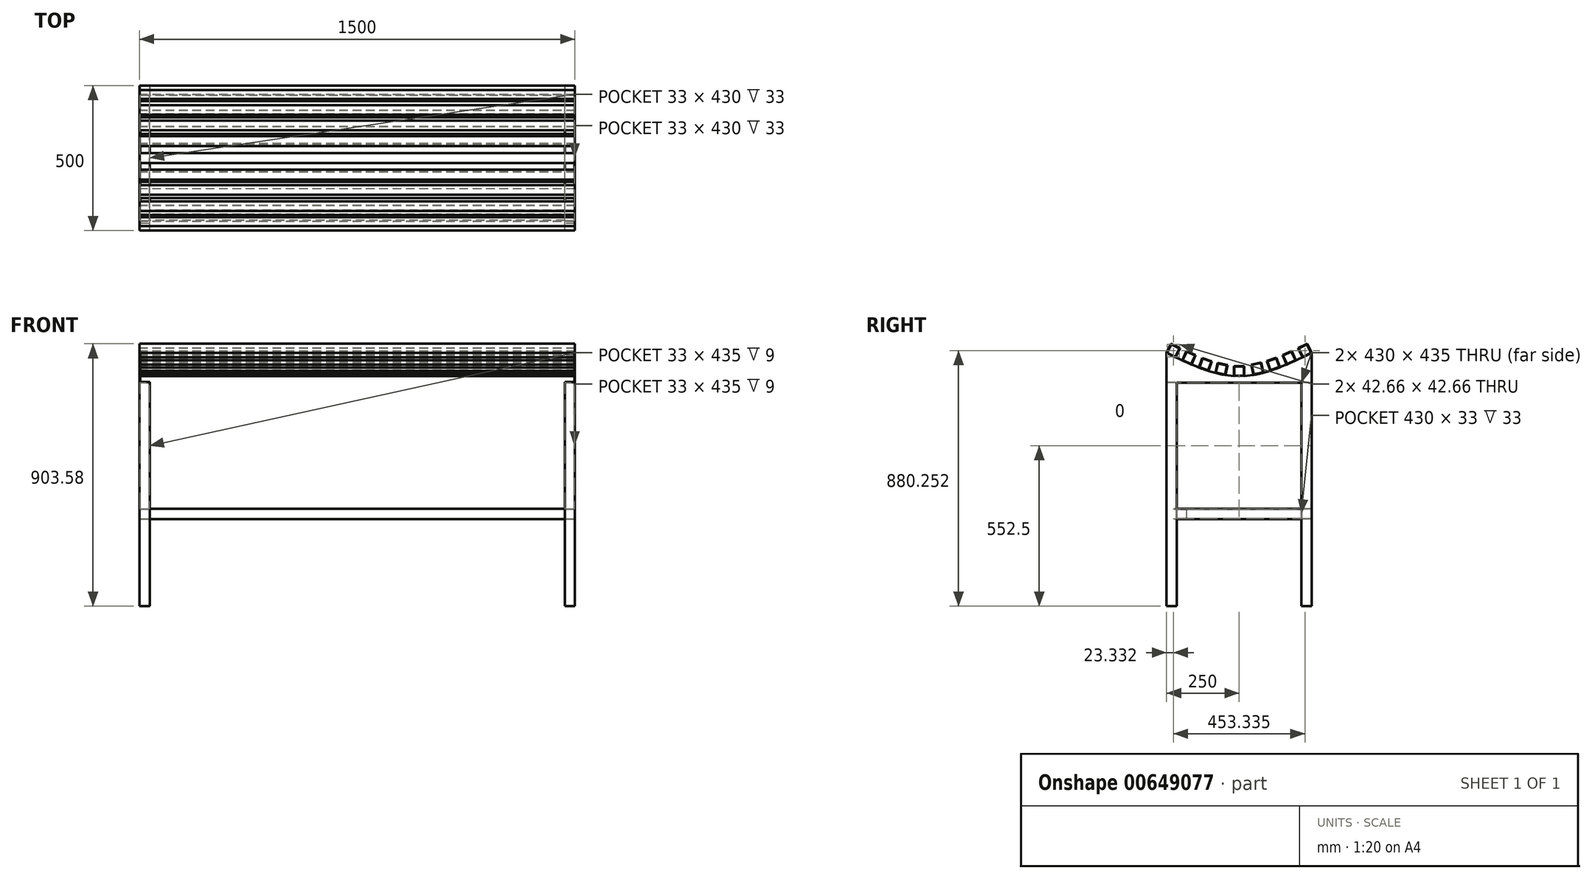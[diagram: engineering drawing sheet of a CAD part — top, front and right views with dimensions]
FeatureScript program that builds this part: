
annotation { "Feature Type Name" : "Feature", "Feature Type Description" : "" }
export const myFeature = defineFeature(function(context is Context, id is Id, definition is map)
    precondition{}
    {
        {
            var Q0;
            Q0=qCreatedBy(makeId("Right.planeOp"),FACE);
            var sketch = newSketch(context, id + "F0", { "sketchPlane" : qUnion([Q0])});
            skLineSegment(sketch, "E0.bottom", {"start": v(-250, -50) * mm, "end": v(250, -50) * mm});
            skLineSegment(sketch, "E0.top", {"start": v(-250, 50) * mm, "end": v(250, 50) * mm});
            skLineSegment(sketch, "E0.left", {"start": v(-250, -50) * mm, "end": v(-250, 50) * mm});
            skLineSegment(sketch, "E0.right", {"start": v(250, -50) * mm, "end": v(250, 50) * mm});
            skPoint(sketch, "E0.middle", {"position": v(0, 0) * mm});
            skLineSegment(sketch, "E1", {"start": v(0, 50) * mm, "end": v(0, -30) * mm, "construction": true});
            skFitSpline(sketch, "E2", {"points": [v(250, 50) * mm, v(0, -30) * mm, v(-250, 50) * mm], "startDerivative": vector(-500, -240) * mm, "endDerivative": vector(-500, 240) * mm});
            skSolve(sketch);
        }
        {
            var Q0;
            Q0=makeQuery(id+"F0.imprint","IMPRINT",FACE,{"disambiguationData":[TD([[makeQuery(id+"F0.imprint","IMPRINT",EDGE,{"derivedFrom":sQuery(id+"F0.wireOp",EDGE,"E0.bottom")}),1.0]])]});
            extrude(context, id + "F1", {"entities" : qUnion([Q0]), "depth" : 2 * mm, "offsetDistance" : 25 * mm});
        }
        {
            var Q0;
            Q0=makeQuery(id+"F1.opExtrude","SWEPT_FACE",FACE,{"disambiguationData":[OSD([sQuery(id+"F0.wireOp",EDGE,"E0.bottom")])]});
            var sketch = newSketch(context, id + "F2", { "sketchPlane" : qUnion([Q0])});
            skLineSegment(sketch, "E3.bottom", {"start": v(0, 250) * mm, "end": v(35, 250) * mm});
            skLineSegment(sketch, "E3.top", {"start": v(0, -250) * mm, "end": v(35, -250) * mm});
            skLineSegment(sketch, "E3.left", {"start": v(0, 250) * mm, "end": v(0, -250) * mm});
            skLineSegment(sketch, "E3.right", {"start": v(35, 250) * mm, "end": v(35, -250) * mm});
            skSolve(sketch);
        }
        {
            var Q0;
            Q0 = qSketchRegion(id + "F2", true);
            extrude(context, id + "F3", {"entities" : qUnion([Q0]), "operationType" : NewBodyOperationType.ADD, "depth" : 2 * mm, "offsetDistance" : 25 * mm});
        }
        {
            var Q0;
            Q0=makeQuery(id+"F1.opExtrude","SWEPT_BODY",BODY,{"disambiguationData":[OSD([sQuery(id+"F0.wireOp",EDGE,"E0.bottom"),sQuery(id+"F0.wireOp",EDGE,"E0.left"),sQuery(id+"F0.wireOp",EDGE,"E0.right"),sQuery(id+"F0.wireOp",EDGE,"E2")])]});
            var Q1;
            Q1=makeQuery(id+"F3.opExtrude","SWEPT_FACE",FACE,{"disambiguationData":[OSD([sQuery(id+"F2.wireOp",EDGE,"E3.right")])]});
            mirror(context, id + "F4", {"entities" : qUnion([Q0]), "mirrorPlane" : qUnion([Q1])});
        }
        {
            var Q0;
            Q0=makeQuery(id+"F4.opPattern","COPY",BODY,{"derivedFrom":makeQuery(id+"F1.opExtrude","SWEPT_BODY",BODY,{"disambiguationData":[OSD([sQuery(id+"F0.wireOp",EDGE,"E0.bottom"),sQuery(id+"F0.wireOp",EDGE,"E0.left"),sQuery(id+"F0.wireOp",EDGE,"E0.right"),sQuery(id+"F0.wireOp",EDGE,"E2")])]}),"instanceName":"1"});
            transform(context, id + "F5", {"entities" : qUnion([Q0]), "transformType" : TransformType.TRANSLATION_3D, "dx" : 1430 * mm, "dy" : 0 * mm, "dz" : 0 * mm, "makeCopy" : false});
        }
        {
            var Q0;
            Q0=makeQuery(id+"F3.boolean.opBoolean","MERGE",FACE,{"derivedFrom":[makeQuery(id+"F1.opExtrude","CAP_FACE",FACE,{"disambiguationData":[OSD([sQuery(id+"F0.wireOp",EDGE,"E0.bottom"),sQuery(id+"F0.wireOp",EDGE,"E0.left"),sQuery(id+"F0.wireOp",EDGE,"E0.right"),sQuery(id+"F0.wireOp",EDGE,"E2")])],"isStart":true}),makeQuery(id+"F3.opExtrude","SWEPT_FACE",FACE,{"disambiguationData":[OSD([sQuery(id+"F2.wireOp",EDGE,"E3.left")])]})]});
            var sketch = newSketch(context, id + "F6", { "sketchPlane" : qUnion([Q0])});
            skLineSegment(sketch, "E4", {"start": v(0, -52) * mm, "end": v(0, -30) * mm, "construction": true});
            skLineSegment(sketch, "E5", {"start": v(0, -30) * mm, "end": v(0, -12.5) * mm, "construction": true});
            skLineSegment(sketch, "E6.bottom", {"start": v(17.5, -30) * mm, "end": v(-17.5, -30) * mm});
            skLineSegment(sketch, "E6.top", {"start": v(17.5, 5) * mm, "end": v(-17.5, 5) * mm});
            skLineSegment(sketch, "E6.left", {"start": v(17.5, -30) * mm, "end": v(17.5, 5) * mm});
            skLineSegment(sketch, "E6.right", {"start": v(-17.5, -30) * mm, "end": v(-17.5, 5) * mm});
            skPoint(sketch, "E6.middle", {"position": v(0, -12.5) * mm});
            skLineSegment(sketch, "E7.bottom", {"start": v(16, -28.5) * mm, "end": v(-16, -28.5) * mm});
            skLineSegment(sketch, "E7.top", {"start": v(16, 3.5) * mm, "end": v(-16, 3.5) * mm});
            skLineSegment(sketch, "E7.left", {"start": v(16, -28.5) * mm, "end": v(16, 3.5) * mm});
            skLineSegment(sketch, "E7.right", {"start": v(-16, -28.5) * mm, "end": v(-16, 3.5) * mm});
            skSolve(sketch);
        }
        {
            var Q0;
            Q0 = qSketchRegion(id + "F6", true);
            extrude(context, id + "F7", {"entities" : qUnion([Q0]), "operationType" : NewBodyOperationType.ADD, "oppositeDirection" : true, "depth" : 1500 * mm, "offsetDistance" : 25 * mm});
        }
        {
            var Q0;
            Q0=makeQuery(id+"F7.boolean.opBoolean","MERGE",FACE,{"derivedFrom":[makeQuery(id+"F3.boolean.opBoolean","MERGE",FACE,{"derivedFrom":[makeQuery(id+"F1.opExtrude","CAP_FACE",FACE,{"disambiguationData":[OSD([sQuery(id+"F0.wireOp",EDGE,"E0.bottom"),sQuery(id+"F0.wireOp",EDGE,"E0.left"),sQuery(id+"F0.wireOp",EDGE,"E0.right"),sQuery(id+"F0.wireOp",EDGE,"E2")])],"isStart":true}),makeQuery(id+"F3.opExtrude","SWEPT_FACE",FACE,{"disambiguationData":[OSD([sQuery(id+"F2.wireOp",EDGE,"E3.left")])]})]}),makeQuery(id+"F7.opExtrude","CAP_FACE",FACE,{"disambiguationData":[OSD([sQuery(id+"F6.wireOp",EDGE,"E6.bottom"),sQuery(id+"F6.wireOp",EDGE,"E6.top"),sQuery(id+"F6.wireOp",EDGE,"E6.left"),sQuery(id+"F6.wireOp",EDGE,"E6.right"),sQuery(id+"F6.wireOp",EDGE,"E7.bottom"),sQuery(id+"F6.wireOp",EDGE,"E7.top"),sQuery(id+"F6.wireOp",EDGE,"E7.left"),sQuery(id+"F6.wireOp",EDGE,"E7.right")])],"isStart":true})]});
            var sketch = newSketch(context, id + "F8", { "sketchPlane" : qUnion([Q0])});
            skLineSegment(sketch, "E8", {"start": v(-250, 50) * mm, "end": v(-218.42, 34.92) * mm});
            skLineSegment(sketch, "E9", {"start": v(-218.42, 34.92) * mm, "end": v(-203.34, 66.5) * mm});
            skLineSegment(sketch, "E10", {"start": v(-203.34, 66.5) * mm, "end": v(-234.92, 81.58) * mm});
            skLineSegment(sketch, "E11", {"start": v(-250, 50) * mm, "end": v(-234.92, 81.58) * mm});
            skLineSegment(sketch, "E12", {"start": v(-250, 50) * mm, "end": v(-203.34, 66.5) * mm, "construction": true});
            skLineSegment(sketch, "E13", {"start": v(-234.92, 81.58) * mm, "end": v(-218.42, 34.92) * mm, "construction": true});
            skLineSegment(sketch, "E14", {"start": v(-219.13, 74.04) * mm, "end": v(-219.77, 72.7) * mm, "construction": true});
            skLineSegment(sketch, "E15", {"start": v(-219.77, 72.7) * mm, "end": v(-234.21, 79.58) * mm});
            skLineSegment(sketch, "E16", {"start": v(-234.21, 79.58) * mm, "end": v(-248, 50.7) * mm});
            skLineSegment(sketch, "E17", {"start": v(-248, 50.7) * mm, "end": v(-219.12, 36.92) * mm});
            skLineSegment(sketch, "E18", {"start": v(-219.12, 36.92) * mm, "end": v(-205.34, 65.8) * mm});
            skLineSegment(sketch, "E19", {"start": v(-205.34, 65.8) * mm, "end": v(-219.77, 72.7) * mm});
            skSolve(sketch);
        }
        {
            var Q0;
            Q0 = qSketchRegion(id + "F8", true);
            extrude(context, id + "F9", {"entities" : qUnion([Q0]), "oppositeDirection" : true, "depth" : 1500 * mm, "offsetDistance" : 25 * mm});
        }
        {
            var Q0;
            Q0=makeQuery(id+"F7.boolean.opBoolean","MERGE",FACE,{"derivedFrom":[makeQuery(id+"F3.boolean.opBoolean","MERGE",FACE,{"derivedFrom":[makeQuery(id+"F1.opExtrude","CAP_FACE",FACE,{"disambiguationData":[OSD([sQuery(id+"F0.wireOp",EDGE,"E0.bottom"),sQuery(id+"F0.wireOp",EDGE,"E0.left"),sQuery(id+"F0.wireOp",EDGE,"E0.right"),sQuery(id+"F0.wireOp",EDGE,"E2")])],"isStart":true}),makeQuery(id+"F3.opExtrude","SWEPT_FACE",FACE,{"disambiguationData":[OSD([sQuery(id+"F2.wireOp",EDGE,"E3.left")])]})]}),makeQuery(id+"F7.opExtrude","CAP_FACE",FACE,{"disambiguationData":[OSD([sQuery(id+"F6.wireOp",EDGE,"E6.bottom"),sQuery(id+"F6.wireOp",EDGE,"E6.top"),sQuery(id+"F6.wireOp",EDGE,"E6.left"),sQuery(id+"F6.wireOp",EDGE,"E6.right"),sQuery(id+"F6.wireOp",EDGE,"E7.bottom"),sQuery(id+"F6.wireOp",EDGE,"E7.top"),sQuery(id+"F6.wireOp",EDGE,"E7.left"),sQuery(id+"F6.wireOp",EDGE,"E7.right")])],"isStart":true})]});
            var sketch = newSketch(context, id + "F10", { "sketchPlane" : qUnion([Q0])});
            skLineSegment(sketch, "E20", {"start": v(-250, 50) * mm, "end": v(-218.42, 34.92) * mm, "construction": true});
            skLineSegment(sketch, "E21", {"start": v(-218.42, 34.92) * mm, "end": v(-195.75, 24.37) * mm, "construction": true});
            skLineSegment(sketch, "E22", {"start": v(-195.75, 24.37) * mm, "end": v(-163.73, 10.23) * mm, "construction": true});
            skLineSegment(sketch, "E23", {"start": v(-163.73, 10.23) * mm, "end": v(-140.57, 0.83) * mm, "construction": true});
            skLineSegment(sketch, "E24", {"start": v(-140.57, 0.83) * mm, "end": v(-107.61, -10.96) * mm, "construction": true});
            skLineSegment(sketch, "E25", {"start": v(-107.61, -10.96) * mm, "end": v(-83.64, -18.07) * mm, "construction": true});
            skLineSegment(sketch, "E26", {"start": v(-83.64, -18.07) * mm, "end": v(-49.47, -25.61) * mm, "construction": true});
            skLineSegment(sketch, "E27", {"start": v(-49.47, -25.61) * mm, "end": v(-41.55, 10.23) * mm});
            skLineSegment(sketch, "E28", {"start": v(-41.55, 10.23) * mm, "end": v(-75.73, 17.78) * mm});
            skLineSegment(sketch, "E29", {"start": v(-75.73, 17.78) * mm, "end": v(-83.64, -18.07) * mm});
            skLineSegment(sketch, "E30", {"start": v(-107.61, -10.96) * mm, "end": v(-95.83, 22) * mm});
            skLineSegment(sketch, "E31", {"start": v(-95.83, 22) * mm, "end": v(-128.79, 33.78) * mm});
            skLineSegment(sketch, "E32", {"start": v(-128.79, 33.78) * mm, "end": v(-140.57, 0.83) * mm});
            skLineSegment(sketch, "E33", {"start": v(-140.57, 0.83) * mm, "end": v(-107.61, -10.96) * mm});
            skLineSegment(sketch, "E34", {"start": v(-195.75, 24.37) * mm, "end": v(-163.73, 10.23) * mm});
            skLineSegment(sketch, "E35", {"start": v(-163.73, 10.23) * mm, "end": v(-149.6, 42.25) * mm});
            skLineSegment(sketch, "E36", {"start": v(-149.6, 42.25) * mm, "end": v(-181.62, 56.39) * mm});
            skLineSegment(sketch, "E37", {"start": v(-181.62, 56.39) * mm, "end": v(-195.75, 24.37) * mm});
            skLineSegment(sketch, "E38", {"start": v(-181.62, 56.39) * mm, "end": v(-163.73, 10.23) * mm, "construction": true});
            skLineSegment(sketch, "E39", {"start": v(-195.75, 24.37) * mm, "end": v(-149.6, 42.25) * mm, "construction": true});
            skLineSegment(sketch, "E40", {"start": v(-128.79, 33.78) * mm, "end": v(-107.61, -10.96) * mm, "construction": true});
            skLineSegment(sketch, "E41", {"start": v(-95.83, 22) * mm, "end": v(-140.57, 0.83) * mm, "construction": true});
            skLineSegment(sketch, "E42", {"start": v(-75.73, 17.78) * mm, "end": v(-49.47, -25.61) * mm, "construction": true});
            skLineSegment(sketch, "E43", {"start": v(-41.55, 10.23) * mm, "end": v(-83.64, -18.07) * mm, "construction": true});
            skLineSegment(sketch, "E44", {"start": v(-165.6, 49.32) * mm, "end": v(-166.17, 47.93) * mm, "construction": true});
            skLineSegment(sketch, "E45", {"start": v(-166.17, 47.93) * mm, "end": v(-151.57, 41.49) * mm});
            skLineSegment(sketch, "E46", {"start": v(-151.57, 41.49) * mm, "end": v(-164.5, 12.21) * mm});
            skLineSegment(sketch, "E47", {"start": v(-164.5, 12.21) * mm, "end": v(-193.77, 25.14) * mm});
            skLineSegment(sketch, "E48", {"start": v(-193.77, 25.14) * mm, "end": v(-180.85, 54.41) * mm});
            skLineSegment(sketch, "E49", {"start": v(-180.85, 54.41) * mm, "end": v(-166.17, 47.93) * mm});
            skLineSegment(sketch, "E50", {"start": v(-112.3, 27.9) * mm, "end": v(-112.81, 26.48) * mm, "construction": true});
            skLineSegment(sketch, "E51", {"start": v(-112.81, 26.48) * mm, "end": v(-97.75, 21.1) * mm});
            skLineSegment(sketch, "E52", {"start": v(-97.75, 21.1) * mm, "end": v(-108.52, -9.04) * mm});
            skLineSegment(sketch, "E53", {"start": v(-108.52, -9.04) * mm, "end": v(-138.65, 1.74) * mm});
            skLineSegment(sketch, "E54", {"start": v(-138.65, 1.74) * mm, "end": v(-127.88, 31.87) * mm});
            skLineSegment(sketch, "E55", {"start": v(-127.88, 31.87) * mm, "end": v(-112.81, 26.48) * mm});
            skLineSegment(sketch, "E56", {"start": v(-58.64, 14) * mm, "end": v(-58.96, 12.54) * mm, "construction": true});
            skLineSegment(sketch, "E57", {"start": v(-58.96, 12.54) * mm, "end": v(-43.27, 9.08) * mm});
            skLineSegment(sketch, "E58", {"start": v(-43.27, 9.08) * mm, "end": v(-50.54, -23.84) * mm});
            skLineSegment(sketch, "E59", {"start": v(-50.54, -23.84) * mm, "end": v(-81.92, -16.9) * mm});
            skLineSegment(sketch, "E60", {"start": v(-81.92, -16.9) * mm, "end": v(-74.66, 16) * mm});
            skLineSegment(sketch, "E61", {"start": v(-74.66, 16) * mm, "end": v(-58.96, 12.54) * mm});
            skSolve(sketch);
        }
        {
            var Q0;
            Q0=makeQuery(id+"F10.imprint","IMPRINT",FACE,{"disambiguationData":[TD([[makeQuery(id+"F10.imprint","IMPRINT",EDGE,{"derivedFrom":sQuery(id+"F10.wireOp",EDGE,"E28")}),1.0]])]});
            var Q1;
            Q1=makeQuery(id+"F10.imprint","IMPRINT",FACE,{"disambiguationData":[TD([[makeQuery(id+"F10.imprint","IMPRINT",EDGE,{"derivedFrom":sQuery(id+"F10.wireOp",EDGE,"E30")}),1.0]])]});
            var Q2;
            Q2=makeQuery(id+"F10.imprint","IMPRINT",FACE,{"disambiguationData":[TD([[makeQuery(id+"F10.imprint","IMPRINT",EDGE,{"derivedFrom":sQuery(id+"F10.wireOp",EDGE,"E34")}),1.0]])]});
            extrude(context, id + "F11", {"entities" : qUnion([Q0, Q1, Q2]), "oppositeDirection" : true, "depth" : 1500 * mm, "offsetDistance" : 25 * mm});
        }
        {
            var Q0;
            Q0=makeQuery(id+"F7.boolean.opBoolean","MERGE",FACE,{"derivedFrom":[makeQuery(id+"F3.boolean.opBoolean","MERGE",FACE,{"derivedFrom":[makeQuery(id+"F1.opExtrude","CAP_FACE",FACE,{"disambiguationData":[OSD([sQuery(id+"F0.wireOp",EDGE,"E0.bottom"),sQuery(id+"F0.wireOp",EDGE,"E0.left"),sQuery(id+"F0.wireOp",EDGE,"E0.right"),sQuery(id+"F0.wireOp",EDGE,"E2")])],"isStart":true}),makeQuery(id+"F3.opExtrude","SWEPT_FACE",FACE,{"disambiguationData":[OSD([sQuery(id+"F2.wireOp",EDGE,"E3.left")])]})]}),makeQuery(id+"F7.opExtrude","CAP_FACE",FACE,{"disambiguationData":[OSD([sQuery(id+"F6.wireOp",EDGE,"E6.bottom"),sQuery(id+"F6.wireOp",EDGE,"E6.top"),sQuery(id+"F6.wireOp",EDGE,"E6.left"),sQuery(id+"F6.wireOp",EDGE,"E6.right"),sQuery(id+"F6.wireOp",EDGE,"E7.bottom"),sQuery(id+"F6.wireOp",EDGE,"E7.top"),sQuery(id+"F6.wireOp",EDGE,"E7.left"),sQuery(id+"F6.wireOp",EDGE,"E7.right")])],"isStart":true})]});
            var sketch = newSketch(context, id + "F12", { "sketchPlane" : qUnion([Q0])});
            skLineSegment(sketch, "E62", {"start": v(250, 50) * mm, "end": v(218.42, 34.92) * mm});
            skLineSegment(sketch, "E63", {"start": v(218.42, 34.92) * mm, "end": v(195.75, 24.37) * mm, "construction": true});
            skLineSegment(sketch, "E64", {"start": v(195.75, 24.37) * mm, "end": v(163.73, 10.23) * mm});
            skLineSegment(sketch, "E65", {"start": v(163.73, 10.23) * mm, "end": v(138.43, 0) * mm, "construction": true});
            skLineSegment(sketch, "E66", {"start": v(138.43, 0) * mm, "end": v(105.42, -11.66) * mm});
            skLineSegment(sketch, "E67", {"start": v(105.42, -11.66) * mm, "end": v(81.42, -18.65) * mm, "construction": true});
            skLineSegment(sketch, "E68", {"start": v(81.42, -18.65) * mm, "end": v(47.2, -26) * mm});
            skLineSegment(sketch, "E69", {"start": v(47.2, -26) * mm, "end": v(39.86, 8.23) * mm});
            skLineSegment(sketch, "E70", {"start": v(39.86, 8.23) * mm, "end": v(74.08, 15.57) * mm});
            skLineSegment(sketch, "E71", {"start": v(74.08, 15.57) * mm, "end": v(81.42, -18.65) * mm});
            skLineSegment(sketch, "E72", {"start": v(105.42, -11.66) * mm, "end": v(93.76, 21.34) * mm});
            skLineSegment(sketch, "E73", {"start": v(93.76, 21.34) * mm, "end": v(126.77, 33) * mm});
            skLineSegment(sketch, "E74", {"start": v(126.77, 33) * mm, "end": v(138.43, 0) * mm});
            skLineSegment(sketch, "E75", {"start": v(163.73, 10.23) * mm, "end": v(149.6, 42.25) * mm});
            skLineSegment(sketch, "E76", {"start": v(149.6, 42.25) * mm, "end": v(181.62, 56.39) * mm});
            skLineSegment(sketch, "E77", {"start": v(181.62, 56.39) * mm, "end": v(195.75, 24.37) * mm});
            skLineSegment(sketch, "E78", {"start": v(218.42, 34.92) * mm, "end": v(203.34, 66.5) * mm});
            skLineSegment(sketch, "E79", {"start": v(203.34, 66.5) * mm, "end": v(234.92, 81.58) * mm});
            skLineSegment(sketch, "E80", {"start": v(234.92, 81.58) * mm, "end": v(250, 50) * mm});
            skLineSegment(sketch, "E81", {"start": v(47.2, -26) * mm, "end": v(74.08, 15.57) * mm, "construction": true});
            skLineSegment(sketch, "E82", {"start": v(81.42, -18.65) * mm, "end": v(39.86, 8.23) * mm, "construction": true});
            skLineSegment(sketch, "E83", {"start": v(105.42, -11.66) * mm, "end": v(126.77, 33) * mm, "construction": true});
            skLineSegment(sketch, "E84", {"start": v(93.76, 21.34) * mm, "end": v(138.43, 0) * mm, "construction": true});
            skLineSegment(sketch, "E85", {"start": v(163.73, 10.23) * mm, "end": v(181.62, 56.39) * mm, "construction": true});
            skLineSegment(sketch, "E86", {"start": v(149.6, 42.25) * mm, "end": v(195.75, 24.37) * mm, "construction": true});
            skLineSegment(sketch, "E87", {"start": v(218.42, 34.92) * mm, "end": v(234.92, 81.58) * mm, "construction": true});
            skLineSegment(sketch, "E88", {"start": v(203.34, 66.5) * mm, "end": v(250, 50) * mm, "construction": true});
            skLineSegment(sketch, "E89", {"start": v(219.13, 74.04) * mm, "end": v(219.77, 72.7) * mm, "construction": true});
            skLineSegment(sketch, "E90", {"start": v(219.77, 72.7) * mm, "end": v(234.21, 79.58) * mm});
            skLineSegment(sketch, "E91", {"start": v(234.21, 79.58) * mm, "end": v(248, 50.7) * mm});
            skLineSegment(sketch, "E92", {"start": v(248, 50.7) * mm, "end": v(219.12, 36.92) * mm});
            skLineSegment(sketch, "E93", {"start": v(219.12, 36.92) * mm, "end": v(205.34, 65.8) * mm});
            skLineSegment(sketch, "E94", {"start": v(205.34, 65.8) * mm, "end": v(219.77, 72.7) * mm});
            skLineSegment(sketch, "E95", {"start": v(165.6, 49.32) * mm, "end": v(166.21, 47.95) * mm, "construction": true});
            skLineSegment(sketch, "E96", {"start": v(166.21, 47.95) * mm, "end": v(180.85, 54.41) * mm});
            skLineSegment(sketch, "E97", {"start": v(180.85, 54.41) * mm, "end": v(193.77, 25.14) * mm});
            skLineSegment(sketch, "E98", {"start": v(193.77, 25.14) * mm, "end": v(164.5, 12.21) * mm});
            skLineSegment(sketch, "E99", {"start": v(164.5, 12.21) * mm, "end": v(151.58, 41.49) * mm});
            skLineSegment(sketch, "E100", {"start": v(151.58, 41.49) * mm, "end": v(166.21, 47.95) * mm});
            skLineSegment(sketch, "E101", {"start": v(110.27, 27.17) * mm, "end": v(110.76, 25.76) * mm, "construction": true});
            skLineSegment(sketch, "E102", {"start": v(110.76, 25.76) * mm, "end": v(125.85, 31.09) * mm});
            skLineSegment(sketch, "E103", {"start": v(125.85, 31.09) * mm, "end": v(136.51, 0.91) * mm});
            skLineSegment(sketch, "E104", {"start": v(136.51, 0.91) * mm, "end": v(106.34, -9.75) * mm});
            skLineSegment(sketch, "E105", {"start": v(106.34, -9.75) * mm, "end": v(95.68, 20.43) * mm});
            skLineSegment(sketch, "E106", {"start": v(95.68, 20.43) * mm, "end": v(110.76, 25.76) * mm});
            skLineSegment(sketch, "E107", {"start": v(56.97, 11.9) * mm, "end": v(57.29, 10.43) * mm, "construction": true});
            skLineSegment(sketch, "E108", {"start": v(57.29, 10.43) * mm, "end": v(72.93, 13.79) * mm});
            skLineSegment(sketch, "E109", {"start": v(72.93, 13.79) * mm, "end": v(79.64, -17.5) * mm});
            skLineSegment(sketch, "E110", {"start": v(79.64, -17.5) * mm, "end": v(48.35, -24.21) * mm});
            skLineSegment(sketch, "E111", {"start": v(48.35, -24.21) * mm, "end": v(41.64, 7.08) * mm});
            skLineSegment(sketch, "E112", {"start": v(41.64, 7.08) * mm, "end": v(57.29, 10.43) * mm});
            skSolve(sketch);
        }
        {
            var Q0;
            Q0 = qSketchRegion(id + "F12", true);
            extrude(context, id + "F13", {"entities" : qUnion([Q0]), "oppositeDirection" : true, "depth" : 1500 * mm, "offsetDistance" : 25 * mm});
        }
        {
            var Q0;
            Q0=makeQuery(id+"F3.opExtrude","CAP_FACE",FACE,{"disambiguationData":[OSD([sQuery(id+"F2.wireOp",EDGE,"E3.bottom"),sQuery(id+"F2.wireOp",EDGE,"E3.top"),sQuery(id+"F2.wireOp",EDGE,"E3.left"),sQuery(id+"F2.wireOp",EDGE,"E3.right")])],"isStart":false});
            var sketch = newSketch(context, id + "F14", { "sketchPlane" : qUnion([Q0])});
            skLineSegment(sketch, "E113", {"start": v(17.5, 250) * mm, "end": v(17.5, 232.5) * mm, "construction": true});
            skLineSegment(sketch, "E114.bottom", {"start": v(0, 250) * mm, "end": v(35, 250) * mm});
            skLineSegment(sketch, "E114.top", {"start": v(0, 215) * mm, "end": v(35, 215) * mm});
            skLineSegment(sketch, "E114.left", {"start": v(0, 250) * mm, "end": v(0, 215) * mm});
            skLineSegment(sketch, "E114.right", {"start": v(35, 250) * mm, "end": v(35, 215) * mm});
            skPoint(sketch, "E114.middle", {"position": v(17.5, 232.5) * mm});
            skLineSegment(sketch, "E115.bottom", {"start": v(1, 216) * mm, "end": v(34, 216) * mm});
            skLineSegment(sketch, "E115.top", {"start": v(1, 249) * mm, "end": v(34, 249) * mm});
            skLineSegment(sketch, "E115.left", {"start": v(1, 216) * mm, "end": v(1, 249) * mm});
            skLineSegment(sketch, "E115.right", {"start": v(34, 216) * mm, "end": v(34, 249) * mm});
            skLineSegment(sketch, "E116", {"start": v(17.5, -250) * mm, "end": v(17.5, -232.5) * mm, "construction": true});
            skLineSegment(sketch, "E117.bottom", {"start": v(35, -250) * mm, "end": v(0, -250) * mm});
            skLineSegment(sketch, "E117.top", {"start": v(35, -215) * mm, "end": v(0, -215) * mm});
            skLineSegment(sketch, "E117.left", {"start": v(35, -250) * mm, "end": v(35, -215) * mm});
            skLineSegment(sketch, "E117.right", {"start": v(0, -250) * mm, "end": v(0, -215) * mm});
            skPoint(sketch, "E117.middle", {"position": v(17.5, -232.5) * mm});
            skLineSegment(sketch, "E118.bottom", {"start": v(34, -249) * mm, "end": v(1, -249) * mm});
            skLineSegment(sketch, "E118.top", {"start": v(34, -216) * mm, "end": v(1, -216) * mm});
            skLineSegment(sketch, "E118.left", {"start": v(34, -249) * mm, "end": v(34, -216) * mm});
            skLineSegment(sketch, "E118.right", {"start": v(1, -249) * mm, "end": v(1, -216) * mm});
            skSolve(sketch);
        }
        {
            var Q0;
            Q0 = qSketchRegion(id + "F14", true);
            extrude(context, id + "F15", {"entities" : qUnion([Q0]), "operationType" : NewBodyOperationType.ADD, "depth" : 770 * mm, "offsetDistance" : 25 * mm});
        }
        {
            var Q0;
            Q0=makeQuery(id+"F4.opPattern","COPY",FACE,{"derivedFrom":makeQuery(id+"F3.opExtrude","CAP_FACE",FACE,{"disambiguationData":[OSD([sQuery(id+"F2.wireOp",EDGE,"E3.bottom"),sQuery(id+"F2.wireOp",EDGE,"E3.top"),sQuery(id+"F2.wireOp",EDGE,"E3.left"),sQuery(id+"F2.wireOp",EDGE,"E3.right")])],"isStart":false}),"instanceName":"1"});
            var sketch = newSketch(context, id + "F16", { "sketchPlane" : qUnion([Q0])});
            skLineSegment(sketch, "E119", {"start": v(1482.5, 250) * mm, "end": v(1482.5, 232.5) * mm, "construction": true});
            skLineSegment(sketch, "E120.bottom", {"start": v(1465, 250) * mm, "end": v(1500, 250) * mm});
            skLineSegment(sketch, "E120.top", {"start": v(1465, 215) * mm, "end": v(1500, 215) * mm});
            skLineSegment(sketch, "E120.left", {"start": v(1465, 250) * mm, "end": v(1465, 215) * mm});
            skLineSegment(sketch, "E120.right", {"start": v(1500, 250) * mm, "end": v(1500, 215) * mm});
            skPoint(sketch, "E120.middle", {"position": v(1482.5, 232.5) * mm});
            skLineSegment(sketch, "E121.bottom", {"start": v(1466, 249) * mm, "end": v(1499, 249) * mm});
            skLineSegment(sketch, "E121.top", {"start": v(1466, 216) * mm, "end": v(1499, 216) * mm});
            skLineSegment(sketch, "E121.left", {"start": v(1466, 249) * mm, "end": v(1466, 216) * mm});
            skLineSegment(sketch, "E121.right", {"start": v(1499, 249) * mm, "end": v(1499, 216) * mm});
            skLineSegment(sketch, "E122", {"start": v(1482.5, -250) * mm, "end": v(1482.5, -232.5) * mm, "construction": true});
            skLineSegment(sketch, "E123.bottom", {"start": v(1500, -250) * mm, "end": v(1465, -250) * mm});
            skLineSegment(sketch, "E123.top", {"start": v(1500, -215) * mm, "end": v(1465, -215) * mm});
            skLineSegment(sketch, "E123.left", {"start": v(1500, -250) * mm, "end": v(1500, -215) * mm});
            skLineSegment(sketch, "E123.right", {"start": v(1465, -250) * mm, "end": v(1465, -215) * mm});
            skPoint(sketch, "E123.middle", {"position": v(1482.5, -232.5) * mm});
            skLineSegment(sketch, "E124.bottom", {"start": v(1466, -216) * mm, "end": v(1499, -216) * mm});
            skLineSegment(sketch, "E124.top", {"start": v(1466, -249) * mm, "end": v(1499, -249) * mm});
            skLineSegment(sketch, "E124.left", {"start": v(1466, -216) * mm, "end": v(1466, -249) * mm});
            skLineSegment(sketch, "E124.right", {"start": v(1499, -216) * mm, "end": v(1499, -249) * mm});
            skSolve(sketch);
        }
        {
            var Q0;
            Q0 = qSketchRegion(id + "F16", true);
            extrude(context, id + "F17", {"entities" : qUnion([Q0]), "operationType" : NewBodyOperationType.ADD, "depth" : 770 * mm, "offsetDistance" : 25 * mm});
        }
        {
            var Q0;
            Q0=makeQuery(id+"F17.opExtrude","SWEPT_FACE",FACE,{"disambiguationData":[OSD([sQuery(id+"F16.wireOp",EDGE,"E123.top")])]});
            var sketch = newSketch(context, id + "F18", { "sketchPlane" : qUnion([Q0])});
            skLineSegment(sketch, "E125", {"start": v(1482.5, -822) * mm, "end": v(1482.5, -522) * mm, "construction": true});
            skLineSegment(sketch, "E126", {"start": v(1482.5, -522) * mm, "end": v(1482.5, -504.5) * mm, "construction": true});
            skLineSegment(sketch, "E127.bottom", {"start": v(1500, -522) * mm, "end": v(1465, -522) * mm});
            skLineSegment(sketch, "E127.top", {"start": v(1500, -487) * mm, "end": v(1465, -487) * mm});
            skLineSegment(sketch, "E127.left", {"start": v(1500, -522) * mm, "end": v(1500, -487) * mm});
            skLineSegment(sketch, "E127.right", {"start": v(1465, -522) * mm, "end": v(1465, -487) * mm});
            skPoint(sketch, "E127.middle", {"position": v(1482.5, -504.5) * mm});
            skLineSegment(sketch, "E128.bottom", {"start": v(1499, -521) * mm, "end": v(1466, -521) * mm});
            skLineSegment(sketch, "E128.top", {"start": v(1499, -488) * mm, "end": v(1466, -488) * mm});
            skLineSegment(sketch, "E128.left", {"start": v(1499, -521) * mm, "end": v(1499, -488) * mm});
            skLineSegment(sketch, "E128.right", {"start": v(1466, -521) * mm, "end": v(1466, -488) * mm});
            skSolve(sketch);
        }
        {
            var Q0;
            Q0 = qSketchRegion(id + "F18", true);
            extrude(context, id + "F19", {"entities" : qUnion([Q0]), "operationType" : NewBodyOperationType.ADD, "depth" : 440 * mm, "offsetDistance" : 25 * mm});
        }
        {
            var Q0;
            Q0=makeQuery(id+"F15.opExtrude","SWEPT_FACE",FACE,{"disambiguationData":[OSD([sQuery(id+"F14.wireOp",EDGE,"E117.top")])]});
            var sketch = newSketch(context, id + "F20", { "sketchPlane" : qUnion([Q0])});
            skLineSegment(sketch, "E129", {"start": v(17.5, -822) * mm, "end": v(17.5, -522) * mm, "construction": true});
            skLineSegment(sketch, "E130", {"start": v(17.5, -522) * mm, "end": v(17.5, -504.5) * mm, "construction": true});
            skLineSegment(sketch, "E131.bottom", {"start": v(35, -522) * mm, "end": v(0, -522) * mm});
            skLineSegment(sketch, "E131.top", {"start": v(35, -487) * mm, "end": v(0, -487) * mm});
            skLineSegment(sketch, "E131.left", {"start": v(35, -522) * mm, "end": v(35, -487) * mm});
            skLineSegment(sketch, "E131.right", {"start": v(0, -522) * mm, "end": v(0, -487) * mm});
            skPoint(sketch, "E131.middle", {"position": v(17.5, -504.5) * mm});
            skLineSegment(sketch, "E132.bottom", {"start": v(34, -488) * mm, "end": v(1, -488) * mm});
            skLineSegment(sketch, "E132.top", {"start": v(34, -521) * mm, "end": v(1, -521) * mm});
            skLineSegment(sketch, "E132.left", {"start": v(34, -488) * mm, "end": v(34, -521) * mm});
            skLineSegment(sketch, "E132.right", {"start": v(1, -488) * mm, "end": v(1, -521) * mm});
            skSolve(sketch);
        }
        {
            var Q0;
            Q0 = qSketchRegion(id + "F20", true);
            extrude(context, id + "F21", {"entities" : qUnion([Q0]), "operationType" : NewBodyOperationType.ADD, "depth" : 440 * mm, "offsetDistance" : 25 * mm});
        }
        {
            var Q0;
            Q0=makeQuery(id+"F21.boolean.opBoolean","MERGE",FACE,{"derivedFrom":[makeQuery(id+"F15.boolean.opBoolean","MERGE",FACE,{"derivedFrom":[makeQuery(id+"F3.opExtrude","SWEPT_FACE",FACE,{"disambiguationData":[OSD([sQuery(id+"F2.wireOp",EDGE,"E3.right")])]}),makeQuery(id+"F15.opExtrude","SWEPT_FACE",FACE,{"disambiguationData":[OSD([sQuery(id+"F14.wireOp",EDGE,"E114.right")])]}),makeQuery(id+"F15.opExtrude","SWEPT_FACE",FACE,{"disambiguationData":[OSD([sQuery(id+"F14.wireOp",EDGE,"E117.left")])]})]}),makeQuery(id+"F21.opExtrude","SWEPT_FACE",FACE,{"disambiguationData":[OSD([sQuery(id+"F20.wireOp",EDGE,"E131.left")])]})]});
            var sketch = newSketch(context, id + "F22", { "sketchPlane" : qUnion([Q0])});
            skLineSegment(sketch, "E133", {"start": v(232.5, -822) * mm, "end": v(232.5, -522) * mm, "construction": true});
            skLineSegment(sketch, "E134", {"start": v(232.5, -522) * mm, "end": v(232.5, -504.5) * mm, "construction": true});
            skLineSegment(sketch, "E135.bottom", {"start": v(250, -522) * mm, "end": v(215, -522) * mm});
            skLineSegment(sketch, "E135.top", {"start": v(250, -487) * mm, "end": v(215, -487) * mm});
            skLineSegment(sketch, "E135.left", {"start": v(250, -522) * mm, "end": v(250, -487) * mm});
            skLineSegment(sketch, "E135.right", {"start": v(215, -522) * mm, "end": v(215, -487) * mm});
            skPoint(sketch, "E135.middle", {"position": v(232.5, -504.5) * mm});
            skLineSegment(sketch, "E136.bottom", {"start": v(249, -488) * mm, "end": v(216, -488) * mm});
            skLineSegment(sketch, "E136.top", {"start": v(249, -521) * mm, "end": v(216, -521) * mm});
            skLineSegment(sketch, "E136.left", {"start": v(249, -488) * mm, "end": v(249, -521) * mm});
            skLineSegment(sketch, "E136.right", {"start": v(216, -488) * mm, "end": v(216, -521) * mm});
            skSolve(sketch);
        }
        {
            var Q0;
            Q0 = qSketchRegion(id + "F22", true);
            extrude(context, id + "F23", {"entities" : qUnion([Q0]), "depth" : 1430 * mm, "offsetDistance" : 25 * mm});
        }
        {
            var Q0;
            Q0=makeQuery(id+"F21.boolean.opBoolean","MERGE",FACE,{"derivedFrom":[makeQuery(id+"F15.boolean.opBoolean","MERGE",FACE,{"derivedFrom":[makeQuery(id+"F3.opExtrude","SWEPT_FACE",FACE,{"disambiguationData":[OSD([sQuery(id+"F2.wireOp",EDGE,"E3.right")])]}),makeQuery(id+"F15.opExtrude","SWEPT_FACE",FACE,{"disambiguationData":[OSD([sQuery(id+"F14.wireOp",EDGE,"E114.right")])]}),makeQuery(id+"F15.opExtrude","SWEPT_FACE",FACE,{"disambiguationData":[OSD([sQuery(id+"F14.wireOp",EDGE,"E117.left")])]})]}),makeQuery(id+"F21.opExtrude","SWEPT_FACE",FACE,{"disambiguationData":[OSD([sQuery(id+"F20.wireOp",EDGE,"E131.left")])]})]});
            var sketch = newSketch(context, id + "F24", { "sketchPlane" : qUnion([Q0])});
            skLineSegment(sketch, "E137", {"start": v(-215, -487) * mm, "end": v(-215, -522) * mm, "construction": true});
            skLineSegment(sketch, "E138", {"start": v(-215, -522) * mm, "end": v(-215, -504.5) * mm, "construction": true});
            skLineSegment(sketch, "E139", {"start": v(-215, -504.5) * mm, "end": v(-197.5, -504.5) * mm, "construction": true});
            skLineSegment(sketch, "E140.bottom", {"start": v(-215, -522) * mm, "end": v(-180, -522) * mm});
            skLineSegment(sketch, "E140.top", {"start": v(-215, -487) * mm, "end": v(-180, -487) * mm});
            skLineSegment(sketch, "E140.left", {"start": v(-215, -522) * mm, "end": v(-215, -487) * mm});
            skLineSegment(sketch, "E140.right", {"start": v(-180, -522) * mm, "end": v(-180, -487) * mm});
            skPoint(sketch, "E140.middle", {"position": v(-197.5, -504.5) * mm});
            skLineSegment(sketch, "E141.bottom", {"start": v(-214, -521) * mm, "end": v(-181, -521) * mm});
            skLineSegment(sketch, "E141.top", {"start": v(-214, -488) * mm, "end": v(-181, -488) * mm});
            skLineSegment(sketch, "E141.left", {"start": v(-214, -521) * mm, "end": v(-214, -488) * mm});
            skLineSegment(sketch, "E141.right", {"start": v(-181, -521) * mm, "end": v(-181, -488) * mm});
            skSolve(sketch);
        }
        {
            var Q0;
            Q0 = qSketchRegion(id + "F24", true);
            extrude(context, id + "F25", {"entities" : qUnion([Q0]), "depth" : 1430 * mm, "offsetDistance" : 25 * mm});
        }
    });
